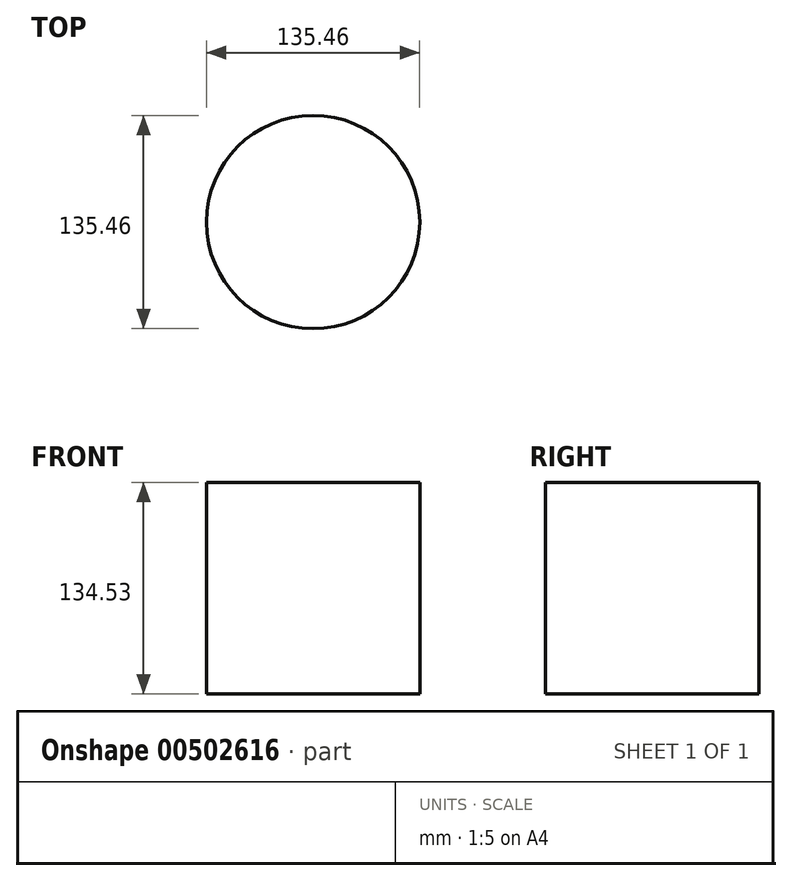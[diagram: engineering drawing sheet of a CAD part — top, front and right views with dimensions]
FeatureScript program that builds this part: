
annotation { "Feature Type Name" : "Feature", "Feature Type Description" : "" }
export const myFeature = defineFeature(function(context is Context, id is Id, definition is map)
    precondition{}
    {
        {
            var Q0;
            Q0=qCreatedBy(makeId("Top.planeOp"),FACE);
            var sketch = newSketch(context, id + "F0", { "sketchPlane" : qUnion([Q0])});
            skCircle(sketch, "E0", {"center": v(0, 0) * mm, "radius": 67.73 * mm});
            skSolve(sketch);
        }
        {
            var Q0;
            Q0=makeQuery(id+"F0.imprint","IMPRINT",FACE,{"disambiguationData":[TD([[makeQuery(id+"F0.imprint","IMPRINT",EDGE,{"derivedFrom":sQuery(id+"F0.wireOp",EDGE,"E0")}),1.0]])]});
            extrude(context, id + "F1", {"entities" : qUnion([Q0]), "depth" : 134.53 * mm});
        }
    });
